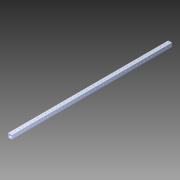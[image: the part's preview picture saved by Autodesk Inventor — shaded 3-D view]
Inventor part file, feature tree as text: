
AUTODESK INVENTOR PART (.ipt)
format: ipt  version: 2014 SP1 (Build 180222100, 222)  size: 1,434,112 bytes
history: native  units: in
note: dims shown in document units (in); Inventor stores cm internally (conversion verified against a paired STEP export)
features: extrude x2, sketch x2, pattern_circular x1, other x1, imported_body x1
ambient origin geometry x8: Origin, YZ Plane, XZ Plane, XY Plane, X Axis, Y Axis, Z Axis, Center Point
bodies: Body1 (feature_tree)
feature tree (7):
  pattern_circular  "CirPattern2"
  other  "1x1 tube1"
  extrude  "Extrusion1"  Depth=0.25in
  extrude  "Extrusion2"  Depth=1.0in
  imported_body  "Base1"
  sketch  "Sketch1"  dims[d0=16.0in d1=0.0in d3=0.25in]
  sketch  "Sketch2"  dims[d4=0.5in d5=21.5in d6=1.0in d7=0.0in]
